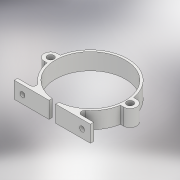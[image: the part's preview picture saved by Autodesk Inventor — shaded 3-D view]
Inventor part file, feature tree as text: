
AUTODESK INVENTOR PART (.ipt)
format: ipt  version: 2018 (Build 220112000, 112)  size: 173,056 bytes
history: native  units: mm
features: extrude x2, sketch x2, mirror x1
ambient origin geometry x8: Origin, YZ Plane, XZ Plane, XY Plane, X Axis, Y Axis, Z Axis, Center Point
bodies: Solid1 (feature_tree)
feature tree (5):
  extrude  "Extrusion1"  Depth=36.0mm
  extrude  "Extrusion2"  Depth=22.55mm
  mirror  "Mirror1"
  sketch  "Sketch1"  dims[d1=23.0mm d2=36.0mm]
  sketch  "Sketch2"  dims[d3=2.0mm d4=1.4mm d5=5.0mm d6=2.0mm d7=4.0mm d8=10.0mm d9=0.0mm d10=3.0mm d11=20.0mm d12=0.0mm d13=42.3mm d14=4.0mm d15=4.0mm d16=48.0mm d17=24.0mm d18=4.0mm d19=22.55mm]
